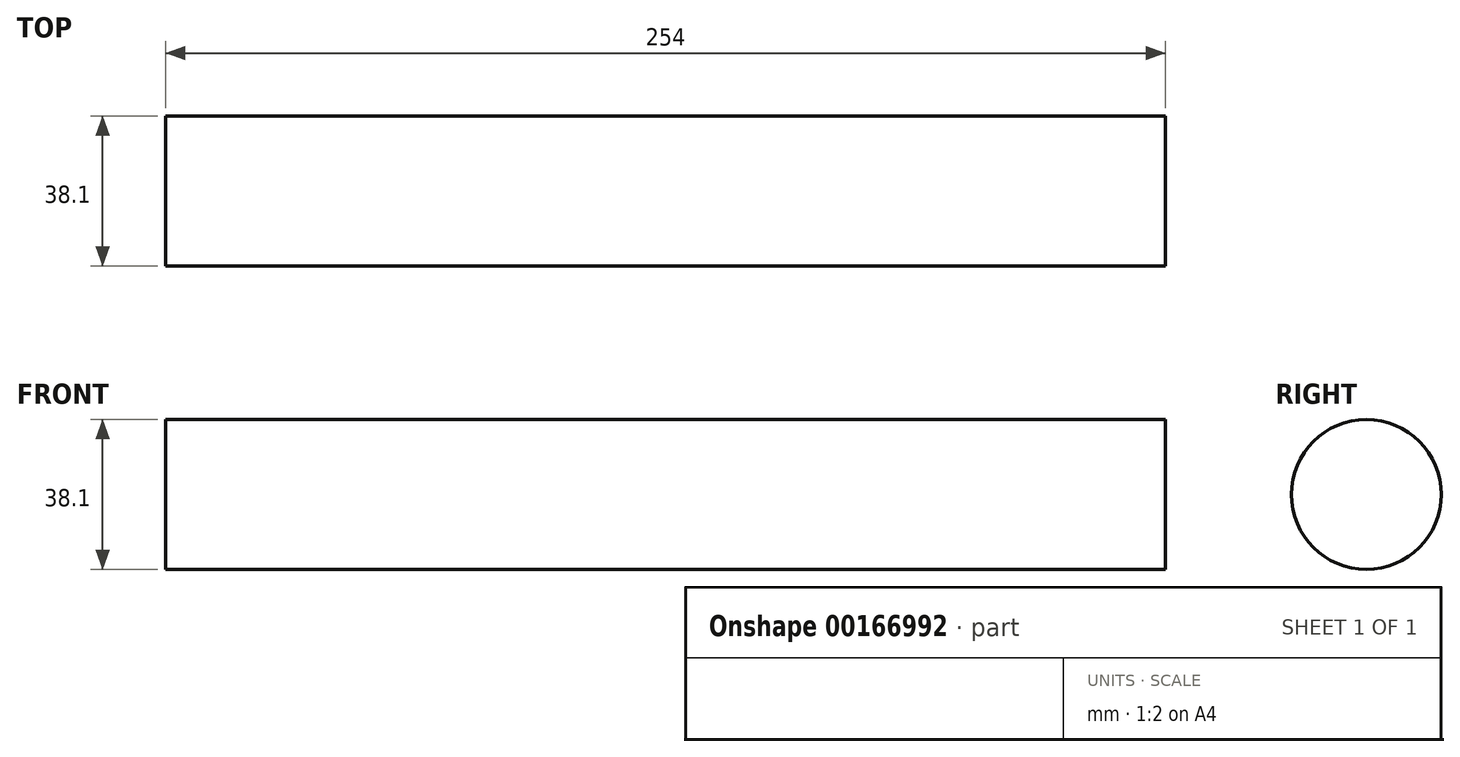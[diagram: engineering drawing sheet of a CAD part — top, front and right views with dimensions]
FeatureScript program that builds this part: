
annotation { "Feature Type Name" : "Feature", "Feature Type Description" : "" }
export const myFeature = defineFeature(function(context is Context, id is Id, definition is map)
    precondition{}
    {
        {
            var Q0;
            Q0=qCreatedBy(makeId("Right.planeOp"),FACE);
            var sketch = newSketch(context, id + "F0", { "sketchPlane" : qUnion([Q0])});
            skCircle(sketch, "E0", {"center": v(0, 0) * mm, "radius": 19.05 * mm});
            skSolve(sketch);
        }
        {
            var Q0;
            Q0 = qSketchRegion(id + "F0", true);
            extrude(context, id + "F1", {"entities" : qUnion([Q0]), "depth" : 254 * mm});
        }
    });
